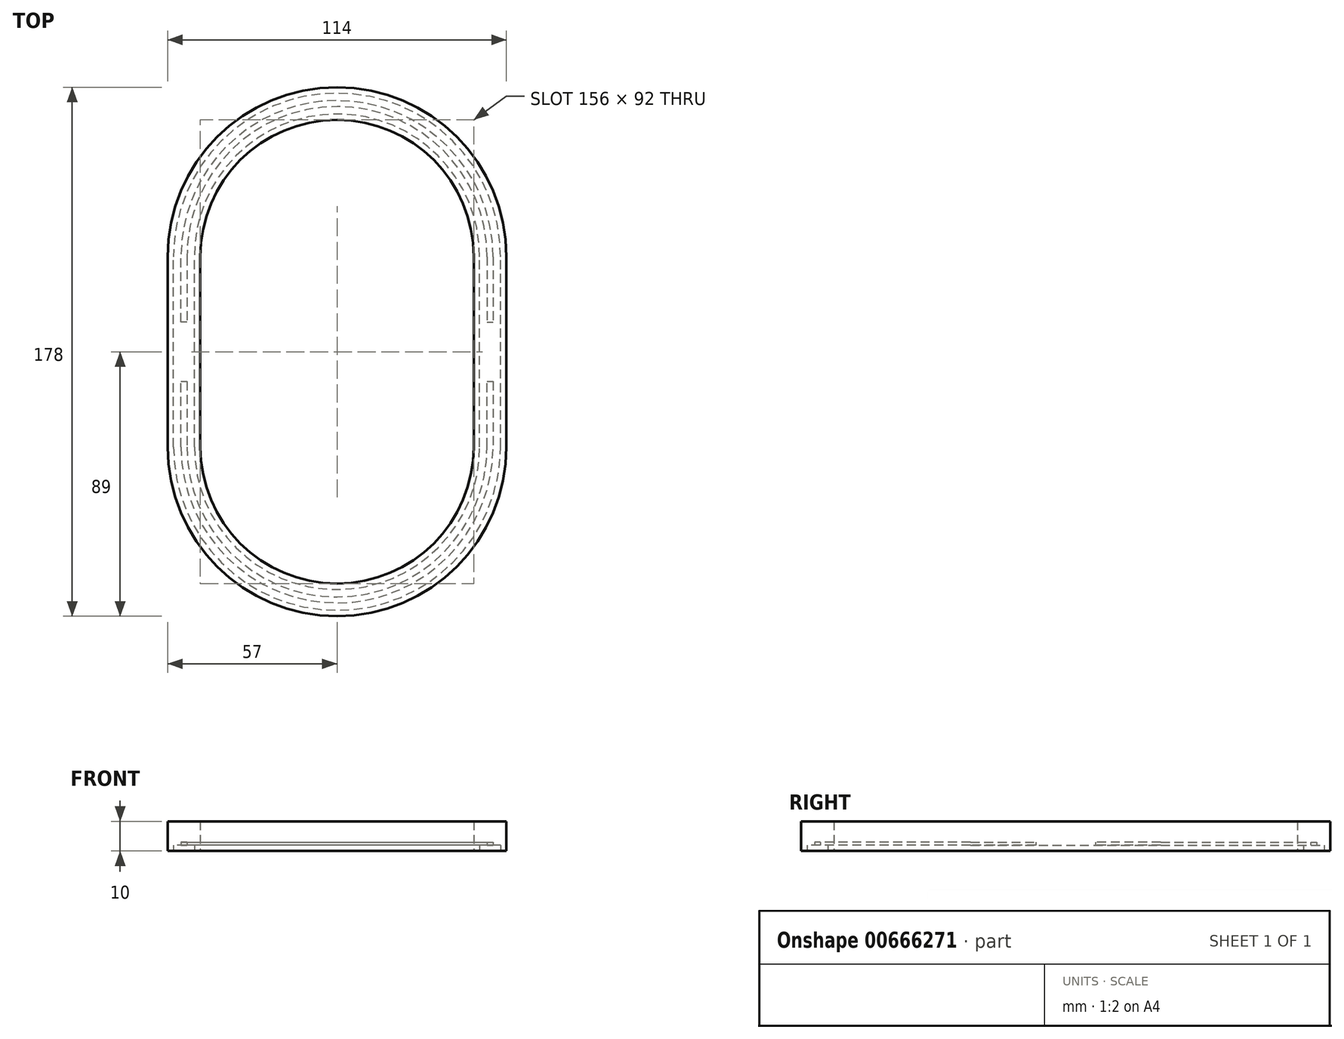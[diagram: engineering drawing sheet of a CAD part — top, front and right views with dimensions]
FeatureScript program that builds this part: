
annotation { "Feature Type Name" : "Feature", "Feature Type Description" : "" }
export const myFeature = defineFeature(function(context is Context, id is Id, definition is map)
    precondition{}
    {
        {
            var Q0;
            Q0=qCreatedBy(makeId("Top.planeOp"),FACE);
            var sketch = newSketch(context, id + "F0", { "sketchPlane" : qUnion([Q0])});
            skLineSegment(sketch, "E0.left", {"start": v(-57, 32) * mm, "end": v(-57, -32) * mm});
            skLineSegment(sketch, "E0.right", {"start": v(57, 32) * mm, "end": v(57, -32) * mm});
            skPoint(sketch, "E0.middle", {"position": v(0, 0) * mm});
            skArc(sketch, "E1", {"start": v(57, 32) * mm, "mid": v(0, 89) * mm, "end": v(-57, 32) * mm});
            skArc(sketch, "E2", {"start": v(-57, -32) * mm, "mid": v(0, -89) * mm, "end": v(57, -32) * mm});
            skLineSegment(sketch, "E3.bottom", {"start": v(-57, 89) * mm, "end": v(57, 89) * mm, "construction": true});
            skLineSegment(sketch, "E3.top", {"start": v(-57, -89) * mm, "end": v(57, -89) * mm, "construction": true});
            skLineSegment(sketch, "E3.left", {"start": v(-57, 89) * mm, "end": v(-57, -89) * mm, "construction": true});
            skLineSegment(sketch, "E3.right", {"start": v(57, 89) * mm, "end": v(57, -89) * mm, "construction": true});
            skArc(sketch, "E4", {"start": v(46, 32) * mm, "mid": v(0, 78) * mm, "end": v(-46, 32) * mm});
            skArc(sketch, "E5", {"start": v(-46, -32) * mm, "mid": v(0, -78) * mm, "end": v(46, -32) * mm});
            skLineSegment(sketch, "E6", {"start": v(-46, 32) * mm, "end": v(-46, -32) * mm});
            skLineSegment(sketch, "E7", {"start": v(46, 32) * mm, "end": v(46, -32) * mm});
            skLineSegment(sketch, "E8.bottom", {"start": v(-46, 78) * mm, "end": v(46, 78) * mm, "construction": true});
            skLineSegment(sketch, "E8.top", {"start": v(-46, -78) * mm, "end": v(46, -78) * mm, "construction": true});
            skLineSegment(sketch, "E8.left", {"start": v(-46, 78) * mm, "end": v(-46, -78) * mm, "construction": true});
            skLineSegment(sketch, "E8.right", {"start": v(46, 78) * mm, "end": v(46, -78) * mm, "construction": true});
            skSolve(sketch);
        }
        {
            var Q0;
            Q0 = qSketchRegion(id + "F0", true);
            extrude(context, id + "F1", {"entities" : qUnion([Q0]), "depth" : 10 * mm, "offsetDistance" : 25 * mm});
        }
        {
            var Q0;
            Q0=makeQuery(id+"F1.opExtrude","CAP_FACE",FACE,{"disambiguationData":[OSD([sQuery(id+"F0.wireOp",EDGE,"E0.left"),sQuery(id+"F0.wireOp",EDGE,"E0.right"),sQuery(id+"F0.wireOp",EDGE,"E1"),sQuery(id+"F0.wireOp",EDGE,"E2"),sQuery(id+"F0.wireOp",EDGE,"E4"),sQuery(id+"F0.wireOp",EDGE,"E5"),sQuery(id+"F0.wireOp",EDGE,"E6"),sQuery(id+"F0.wireOp",EDGE,"E7")])],"isStart":true});
            var sketch = newSketch(context, id + "F2", { "sketchPlane" : qUnion([Q0])});
            skLineSegment(sketch, "E9.bottom", {"start": v(-48, 32) * mm, "end": v(48, 32) * mm, "construction": true});
            skLineSegment(sketch, "E9.top", {"start": v(-48, -32) * mm, "end": v(48, -32) * mm, "construction": true});
            skLineSegment(sketch, "E9.left", {"start": v(-48, 32) * mm, "end": v(-48, -32) * mm});
            skLineSegment(sketch, "E9.right", {"start": v(48, 32) * mm, "end": v(48, -32) * mm});
            skPoint(sketch, "E9.middle", {"position": v(0, 0) * mm});
            skLineSegment(sketch, "E10.bottom", {"start": v(-55, 32) * mm, "end": v(55, 32) * mm, "construction": true});
            skLineSegment(sketch, "E10.top", {"start": v(-55, -32) * mm, "end": v(55, -32) * mm, "construction": true});
            skLineSegment(sketch, "E10.left", {"start": v(-55, 32) * mm, "end": v(-55, -32) * mm});
            skLineSegment(sketch, "E10.right", {"start": v(55, 32) * mm, "end": v(55, -32) * mm});
            skArc(sketch, "E11", {"start": v(48, 32) * mm, "mid": v(0, 80) * mm, "end": v(-48, 32) * mm});
            skArc(sketch, "E12", {"start": v(55, 32) * mm, "mid": v(0, 87) * mm, "end": v(-55, 32) * mm});
            skArc(sketch, "E13", {"start": v(-48, -32) * mm, "mid": v(0, -80) * mm, "end": v(48, -32) * mm});
            skArc(sketch, "E14", {"start": v(-55, -32) * mm, "mid": v(0, -87) * mm, "end": v(55, -32) * mm});
            skSolve(sketch);
        }
        {
            var Q0;
            Q0 = qSketchRegion(id + "F2", true);
            extrude(context, id + "F3", {"entities" : qUnion([Q0]), "operationType" : NewBodyOperationType.REMOVE, "oppositeDirection" : true, "depth" : 2 * mm, "offsetDistance" : 25 * mm});
        }
        {
            var Q0;
            Q0=makeQuery(id+"F3.boolean.opBoolean","COPY",FACE,{"derivedFrom":makeQuery(id+"F3.opExtrude","CAP_FACE",FACE,{"disambiguationData":[OSD([sQuery(id+"F2.wireOp",EDGE,"E9.left"),sQuery(id+"F2.wireOp",EDGE,"E9.right"),sQuery(id+"F2.wireOp",EDGE,"E10.left"),sQuery(id+"F2.wireOp",EDGE,"E10.right"),sQuery(id+"F2.wireOp",EDGE,"E11"),sQuery(id+"F2.wireOp",EDGE,"E12"),sQuery(id+"F2.wireOp",EDGE,"E13"),sQuery(id+"F2.wireOp",EDGE,"E14")])],"isStart":false})});
            var sketch = newSketch(context, id + "F4", { "sketchPlane" : qUnion([Q0])});
            skLineSegment(sketch, "E15.bottom", {"start": v(-52.5, 32) * mm, "end": v(52.5, 32) * mm, "construction": true});
            skLineSegment(sketch, "E15.top", {"start": v(-52.5, -32) * mm, "end": v(52.5, -32) * mm, "construction": true});
            skLineSegment(sketch, "E15.left", {"start": v(-52.5, 32) * mm, "end": v(-52.5, -32) * mm, "construction": true});
            skLineSegment(sketch, "E15.right", {"start": v(52.5, 32) * mm, "end": v(52.5, -32) * mm, "construction": true});
            skPoint(sketch, "E15.middle", {"position": v(0, 0) * mm});
            skLineSegment(sketch, "E16.bottom", {"start": v(-50.5, 32) * mm, "end": v(50.5, 32) * mm, "construction": true});
            skLineSegment(sketch, "E16.top", {"start": v(-50.5, -32) * mm, "end": v(50.5, -32) * mm, "construction": true});
            skLineSegment(sketch, "E16.left", {"start": v(-50.5, 32) * mm, "end": v(-50.5, -32) * mm, "construction": true});
            skLineSegment(sketch, "E16.right", {"start": v(50.5, 32) * mm, "end": v(50.5, -32) * mm, "construction": true});
            skArc(sketch, "E17", {"start": v(52.5, 32) * mm, "mid": v(0, 84.5) * mm, "end": v(-52.5, 32) * mm});
            skArc(sketch, "E18", {"start": v(50.5, 32) * mm, "mid": v(0, 82.5) * mm, "end": v(-50.5, 32) * mm});
            skArc(sketch, "E19", {"start": v(-52.5, -32) * mm, "mid": v(0, -84.5) * mm, "end": v(52.5, -32) * mm});
            skArc(sketch, "E20", {"start": v(-50.5, -32) * mm, "mid": v(0, -82.5) * mm, "end": v(50.5, -32) * mm});
            skLineSegment(sketch, "E21", {"start": v(-52.5, 32) * mm, "end": v(-52.5, 10) * mm});
            skLineSegment(sketch, "E22", {"start": v(-52.5, 10) * mm, "end": v(-50.5, 10) * mm});
            skLineSegment(sketch, "E23", {"start": v(-50.5, 10) * mm, "end": v(-50.5, 32) * mm});
            skLineSegment(sketch, "E24", {"start": v(-50.5, -32) * mm, "end": v(-50.5, -10) * mm});
            skLineSegment(sketch, "E25", {"start": v(-50.5, -10) * mm, "end": v(-52.5, -10) * mm});
            skLineSegment(sketch, "E26", {"start": v(-52.5, -10) * mm, "end": v(-52.5, -32) * mm});
            skLineSegment(sketch, "E27", {"start": v(50.5, 32) * mm, "end": v(50.5, 10) * mm});
            skLineSegment(sketch, "E28", {"start": v(50.5, 10) * mm, "end": v(52.5, 10) * mm});
            skLineSegment(sketch, "E29", {"start": v(52.5, 10) * mm, "end": v(52.5, 32) * mm});
            skLineSegment(sketch, "E30", {"start": v(52.5, -32) * mm, "end": v(52.5, -10) * mm});
            skLineSegment(sketch, "E31", {"start": v(50.5, -32) * mm, "end": v(50.5, -10) * mm});
            skLineSegment(sketch, "E32", {"start": v(50.5, -10) * mm, "end": v(52.5, -10) * mm});
            skSolve(sketch);
        }
        {
            var Q0;
            Q0 = qSketchRegion(id + "F4", true);
            extrude(context, id + "F5", {"entities" : qUnion([Q0]), "operationType" : NewBodyOperationType.REMOVE, "oppositeDirection" : true, "depth" : 1 * mm, "offsetDistance" : 25 * mm});
        }
    });
